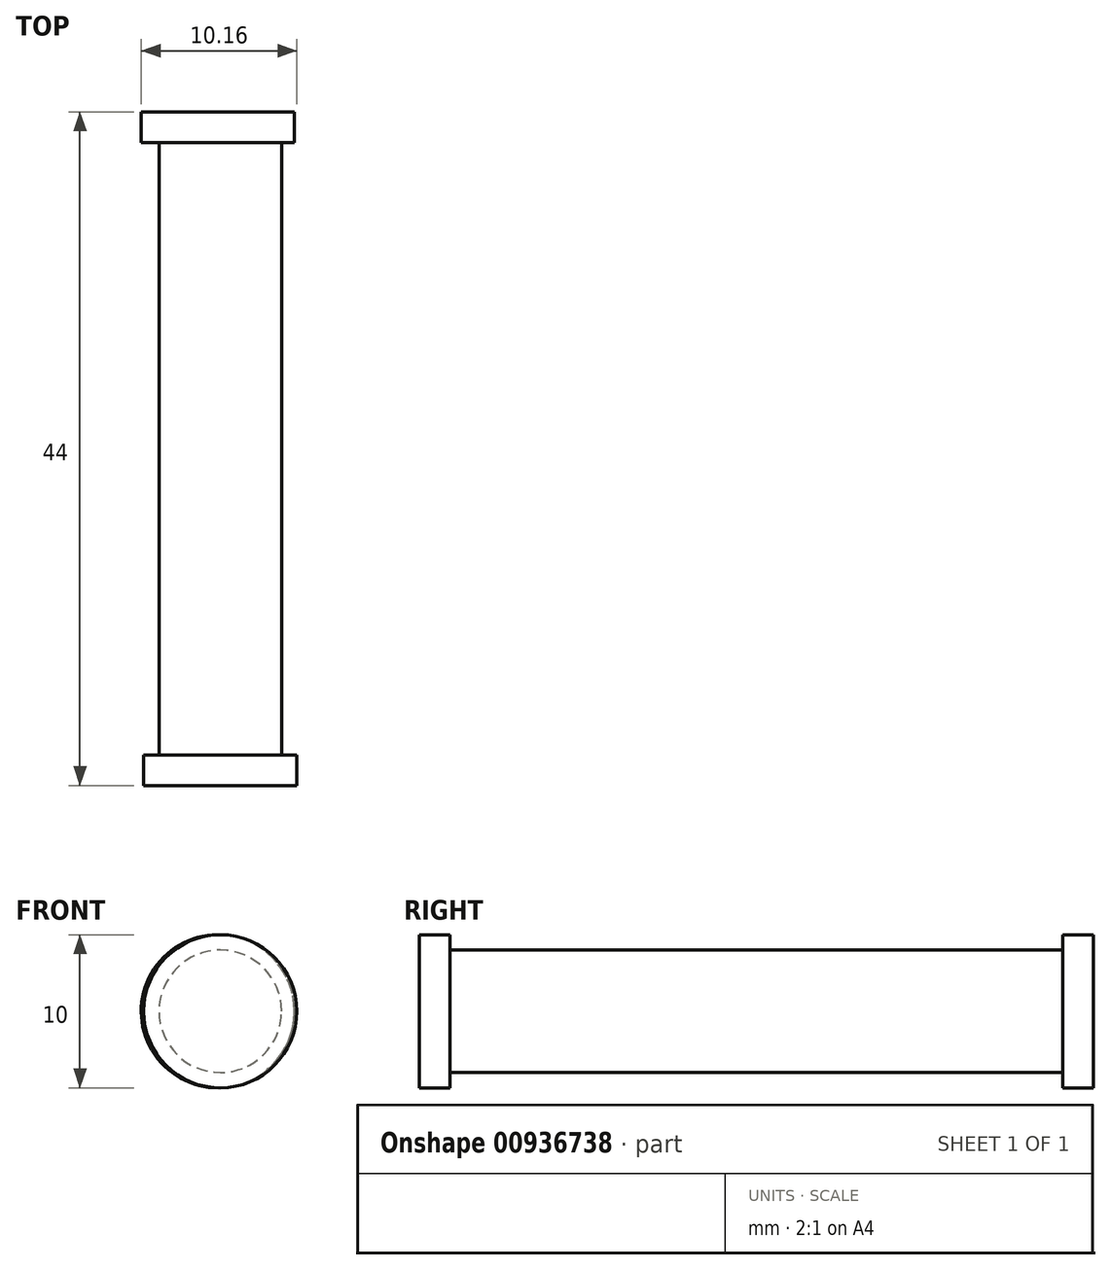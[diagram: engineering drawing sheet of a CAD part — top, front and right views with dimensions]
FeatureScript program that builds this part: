
annotation { "Feature Type Name" : "Feature", "Feature Type Description" : "" }
export const myFeature = defineFeature(function(context is Context, id is Id, definition is map)
    precondition{}
    {
        {
            var Q0;
            Q0=qCreatedBy(makeId("Front.planeOp"),FACE);
            var sketch = newSketch(context, id + "F0", { "sketchPlane" : qUnion([Q0])});
            skCircle(sketch, "E0", {"center": v(0, 0) * mm, "radius": 4 * mm});
            skSolve(sketch);
        }
        {
            var Q0;
            Q0=makeQuery(id+"F0.imprint","IMPRINT",FACE,{"disambiguationData":[TD([[makeQuery(id+"F0.imprint","IMPRINT",EDGE,{"derivedFrom":sQuery(id+"F0.wireOp",EDGE,"E0")}),1.0]])]});
            extrude(context, id + "F1", {"entities" : qUnion([Q0]), "depth" : 40 * mm, "offsetDistance" : 25 * mm});
        }
        {
            var Q0;
            Q0=makeQuery(id+"F1.opExtrude","CAP_FACE",FACE,{"disambiguationData":[OSD([sQuery(id+"F0.wireOp",EDGE,"E0")])],"isStart":false});
            var sketch = newSketch(context, id + "F2", { "sketchPlane" : qUnion([Q0])});
            skCircle(sketch, "E1", {"center": v(0, 0) * mm, "radius": 5 * mm});
            skSolve(sketch);
        }
        {
            var Q0;
            Q0=makeQuery(id+"F2.imprint","IMPRINT",FACE,{"disambiguationData":[TD([[makeQuery(id+"F2.imprint","IMPRINT",EDGE,{"derivedFrom":makeQuery(id+"F1.opExtrude","CAP_EDGE",EDGE,{"disambiguationData":[OSD([sQuery(id+"F0.wireOp",EDGE,"E0")])],"isStart":false})}),1.0]])]});
            var Q1;
            Q1=makeQuery(id+"F2.imprint","IMPRINT",FACE,{"disambiguationData":[TD([[makeQuery(id+"F2.imprint","IMPRINT",EDGE,{"derivedFrom":sQuery(id+"F2.wireOp",EDGE,"E1")}),1.0]])]});
            extrude(context, id + "F3", {"entities" : qUnion([Q0, Q1]), "operationType" : NewBodyOperationType.ADD, "depth" : 2 * mm, "offsetDistance" : 25 * mm});
        }
        {
            var Q0;
            Q0=makeQuery(id+"F1.opExtrude","CAP_FACE",FACE,{"disambiguationData":[OSD([sQuery(id+"F0.wireOp",EDGE,"E0")])],"isStart":true});
            var sketch = newSketch(context, id + "F4", { "sketchPlane" : qUnion([Q0])});
            skCircle(sketch, "E2", {"center": v(0.16, 0) * mm, "radius": 5 * mm});
            skSolve(sketch);
        }
        {
            var Q0;
            Q0=makeQuery(id+"F4.imprint","IMPRINT",FACE,{"disambiguationData":[TD([[makeQuery(id+"F4.imprint","IMPRINT",EDGE,{"derivedFrom":makeQuery(id+"F1.opExtrude","CAP_EDGE",EDGE,{"disambiguationData":[OSD([sQuery(id+"F0.wireOp",EDGE,"E0")])],"isStart":true})}),-1.0]])]});
            var Q1;
            Q1=makeQuery(id+"F4.imprint","IMPRINT",FACE,{"disambiguationData":[TD([[makeQuery(id+"F4.imprint","IMPRINT",EDGE,{"derivedFrom":sQuery(id+"F4.wireOp",EDGE,"E2")}),1.0]])]});
            extrude(context, id + "F5", {"entities" : qUnion([Q0, Q1]), "operationType" : NewBodyOperationType.ADD, "depth" : 2 * mm, "offsetDistance" : 25 * mm});
        }
    });
